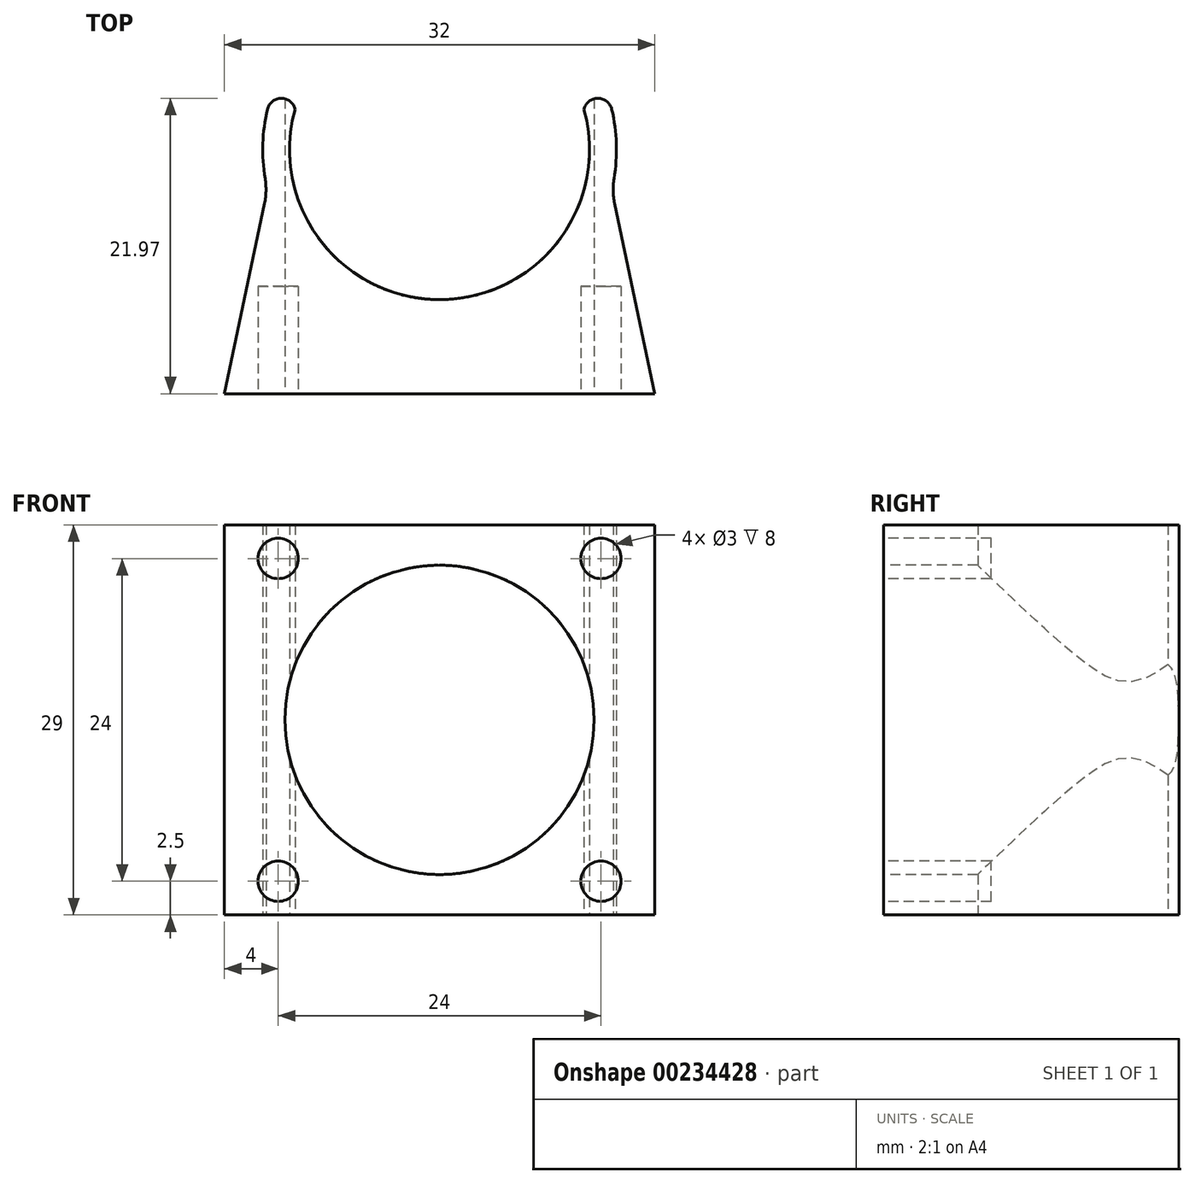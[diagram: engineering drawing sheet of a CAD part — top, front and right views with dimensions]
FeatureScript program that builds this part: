
annotation { "Feature Type Name" : "Feature", "Feature Type Description" : "" }
export const myFeature = defineFeature(function(context is Context, id is Id, definition is map)
    precondition{}
    {
        {
            var Q0;
            Q0=qCreatedBy(makeId("Top.planeOp"),FACE);
            var sketch = newSketch(context, id + "F0", { "sketchPlane" : qUnion([Q0])});
            skArc(sketch, "E0", {"start": v(-10.74, 3) * mm, "mid": v(0, -11.15) * mm, "end": v(10.74, 3) * mm});
            skArc(sketch, "E1.0", {"start": v(-12.8, 3) * mm, "mid": v(-13.14, 0.43) * mm, "end": v(-12.97, -2.15) * mm});
            skArc(sketch, "E2", {"start": v(-12.8, 3) * mm, "mid": v(-11.77, 3.82) * mm, "end": v(-10.74, 3) * mm});
            skArc(sketch, "E3", {"start": v(12.8, 3) * mm, "mid": v(11.77, 3.82) * mm, "end": v(10.74, 3) * mm});
            skPoint(sketch, "E4.left.start.orphan", {"position": v(0, -13.15) * mm});
            skPoint(sketch, "E5.start.orphan", {"position": v(-12.8, -3) * mm});
            skLineSegment(sketch, "E6", {"start": v(0, -18.15) * mm, "end": v(16, -18.15) * mm});
            skPoint(sketch, "E6.startSnap0", {"position": v(0, -11.15) * mm});
            skLineSegment(sketch, "E7", {"start": v(0, -18.15) * mm, "end": v(-16, -18.15) * mm});
            skLineSegment(sketch, "E8", {"start": v(-13.01, -4) * mm, "end": v(-16, -18.15) * mm});
            skLineSegment(sketch, "E9", {"start": v(16, -18.15) * mm, "end": v(13.01, -4) * mm});
            skArc(sketch, "E10.trimOffspring", {"start": v(12.97, -2.15) * mm, "mid": v(13.14, 0.43) * mm, "end": v(12.8, 3) * mm});
            skArc(sketch, "E11.filletArc", {"start": v(-13.01, -4) * mm, "mid": v(-12.9, -3.08) * mm, "end": v(-12.97, -2.15) * mm});
            skPoint(sketch, "E12.visualSharp", {"position": v(12.8, -3) * mm});
            skArc(sketch, "E12.filletArc", {"start": v(12.97, -2.15) * mm, "mid": v(12.9, -3.08) * mm, "end": v(13.01, -4) * mm});
            skSolve(sketch);
        }
        {
            var Q0;
            Q0=makeQuery(id+"F0.imprint","IMPRINT",FACE,{"disambiguationData":[TD([[makeQuery(id+"F0.imprint","IMPRINT",EDGE,{"derivedFrom":sQuery(id+"F0.wireOp",EDGE,"E0")}),-1.0]])]});
            var Q1;
            Q1=makeQuery(id+"F0.imprint","IMPRINT",FACE,{"disambiguationData":[TD([[makeQuery(id+"F0.imprint","IMPRINT",EDGE,{"derivedFrom":sQuery(id+"F0.wireOp",EDGE,"E4.top")}),-1.0]])]});
            extrude(context, id + "F1", {"entities" : qUnion([Q0, Q1]), "depth" : 29 * mm});
        }
        {
            var Q0;
            Q0=makeQuery(id+"F1.opExtrude","SWEPT_FACE",FACE,{"disambiguationData":[OSD([sQuery(id+"F0.wireOp",EDGE,"E6"),sQuery(id+"F0.wireOp",EDGE,"E7")])]});
            var sketch = newSketch(context, id + "F2", { "sketchPlane" : qUnion([Q0])});
            skCircle(sketch, "E13", {"center": v(0, 14.5) * mm, "radius": 11.5 * mm});
            skPoint(sketch, "E13.centerSnap0", {"position": v(16, 14.5) * mm});
            skCircle(sketch, "E14", {"center": v(12, 2.5) * mm, "radius": 1.5 * mm});
            skCircle(sketch, "E15", {"center": v(-12, 2.5) * mm, "radius": 1.5 * mm});
            skCircle(sketch, "E16", {"center": v(-12, 26.5) * mm, "radius": 1.5 * mm});
            skCircle(sketch, "E17", {"center": v(12, 26.5) * mm, "radius": 1.5 * mm});
            skSolve(sketch);
        }
        {
            var Q0;
            Q0=makeQuery(id+"F2.imprint","IMPRINT",FACE,{"disambiguationData":[TD([[makeQuery(id+"F2.imprint","IMPRINT",EDGE,{"derivedFrom":sQuery(id+"F2.wireOp",EDGE,"E13")}),1.0]])]});
            extrude(context, id + "F3", {"entities" : qUnion([Q0]), "operationType" : NewBodyOperationType.REMOVE, "oppositeDirection" : true, "depth" : 25 * mm});
        }
        {
            var Q0;
            Q0=makeQuery(id+"F2.imprint","IMPRINT",FACE,{"disambiguationData":[TD([[makeQuery(id+"F2.imprint","IMPRINT",EDGE,{"derivedFrom":sQuery(id+"F2.wireOp",EDGE,"E16")}),1.0]])]});
            var Q1;
            Q1=makeQuery(id+"F2.imprint","IMPRINT",FACE,{"disambiguationData":[TD([[makeQuery(id+"F2.imprint","IMPRINT",EDGE,{"derivedFrom":sQuery(id+"F2.wireOp",EDGE,"E15")}),1.0]])]});
            var Q2;
            Q2=makeQuery(id+"F2.imprint","IMPRINT",FACE,{"disambiguationData":[TD([[makeQuery(id+"F2.imprint","IMPRINT",EDGE,{"derivedFrom":sQuery(id+"F2.wireOp",EDGE,"E17")}),1.0]])]});
            var Q3;
            Q3=makeQuery(id+"F2.imprint","IMPRINT",FACE,{"disambiguationData":[TD([[makeQuery(id+"F2.imprint","IMPRINT",EDGE,{"derivedFrom":sQuery(id+"F2.wireOp",EDGE,"E14")}),1.0]])]});
            extrude(context, id + "F4", {"entities" : qUnion([Q0, Q1, Q2, Q3]), "operationType" : NewBodyOperationType.REMOVE, "oppositeDirection" : true, "depth" : 8 * mm});
        }
    });
